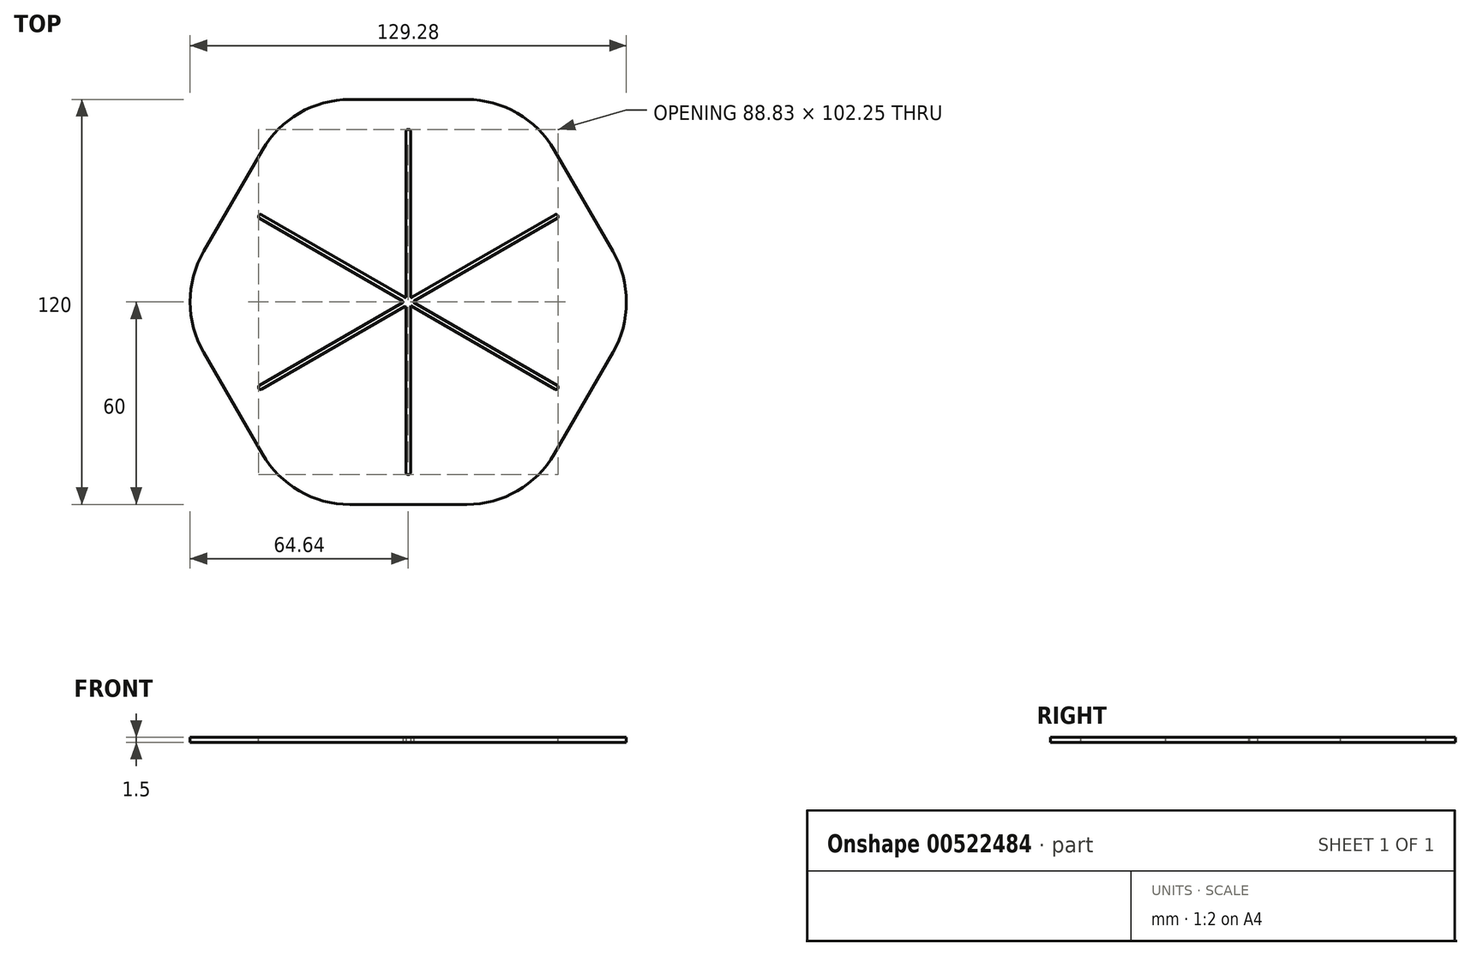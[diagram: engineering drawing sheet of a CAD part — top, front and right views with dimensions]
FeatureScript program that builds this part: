
annotation { "Feature Type Name" : "Feature", "Feature Type Description" : "" }
export const myFeature = defineFeature(function(context is Context, id is Id, definition is map)
    precondition{}
    {
        {
            var Q0;
            Q0=qCreatedBy(makeId("Top.planeOp"),FACE);
            var sketch = newSketch(context, id + "F0", { "sketchPlane" : qUnion([Q0])});
            skCircle(sketch, "E0.cCircle", {"center": v(0, 0) * mm, "radius": 60 * mm, "construction": true});
            skLineSegment(sketch, "E0.0", {"start": v(-34.64, 60) * mm, "end": v(34.64, 60) * mm});
            skLineSegment(sketch, "E0.1", {"start": v(34.64, 60) * mm, "end": v(69.28, 0) * mm});
            skLineSegment(sketch, "E0.2", {"start": v(69.28, 0) * mm, "end": v(34.64, -60) * mm});
            skLineSegment(sketch, "E0.3", {"start": v(34.64, -60) * mm, "end": v(-34.64, -60) * mm});
            skLineSegment(sketch, "E0.4", {"start": v(-34.64, -60) * mm, "end": v(-69.28, 0) * mm});
            skLineSegment(sketch, "E0.5", {"start": v(-69.28, 0) * mm, "end": v(-34.64, 60) * mm});
            skPoint(sketch, "E0.0.midPoint", {"position": v(0, 60) * mm});
            skLineSegment(sketch, "E1.bottom", {"start": v(0.65, -51.13) * mm, "end": v(-0.65, -51.13) * mm});
            skLineSegment(sketch, "E1.top", {"start": v(0.65, 51.13) * mm, "end": v(-0.65, 51.13) * mm});
            skLineSegment(sketch, "E1.left", {"start": v(0.65, -51.13) * mm, "end": v(0.65, -1.13) * mm});
            skLineSegment(sketch, "E1.right", {"start": v(-0.65, -51.13) * mm, "end": v(-0.65, -1.13) * mm});
            skLineSegment(sketch, "E2.1.1", {"start": v(43.95, 26.13) * mm, "end": v(0.65, 1.13) * mm});
            skLineSegment(sketch, "E2.1.2", {"start": v(44.6, 25) * mm, "end": v(1.3, 0) * mm});
            skLineSegment(sketch, "E2.1.3", {"start": v(43.95, 26.13) * mm, "end": v(44.6, 25) * mm});
            skLineSegment(sketch, "E2.1.4", {"start": v(-44.6, -25) * mm, "end": v(-43.95, -26.13) * mm});
            skLineSegment(sketch, "E2.2.1", {"start": v(-44.6, 25) * mm, "end": v(-1.3, 0) * mm});
            skLineSegment(sketch, "E2.2.2", {"start": v(-43.95, 26.13) * mm, "end": v(-0.65, 1.13) * mm});
            skLineSegment(sketch, "E2.2.3", {"start": v(-44.6, 25) * mm, "end": v(-43.95, 26.13) * mm});
            skLineSegment(sketch, "E2.2.4", {"start": v(43.95, -26.13) * mm, "end": v(44.6, -25) * mm});
            skLineSegment(sketch, "E3.trimOffspring", {"start": v(1.3, 0) * mm, "end": v(44.6, -25) * mm});
            skLineSegment(sketch, "E4.trimOffspring", {"start": v(0.65, 1.13) * mm, "end": v(0.65, 51.13) * mm});
            skLineSegment(sketch, "E5.trimOffspring", {"start": v(-1.3, 0) * mm, "end": v(-44.6, -25) * mm});
            skLineSegment(sketch, "E6.trimOffspring", {"start": v(-0.65, 1.13) * mm, "end": v(-0.65, 51.13) * mm});
            skLineSegment(sketch, "E7.trimOffspring", {"start": v(0.65, -1.13) * mm, "end": v(43.95, -26.13) * mm});
            skLineSegment(sketch, "E8.trimOffspring", {"start": v(-0.65, -1.13) * mm, "end": v(-43.95, -26.13) * mm});
            skSolve(sketch);
        }
        {
            var Q0;
            Q0 = qSketchRegion(id + "F0", true);
            extrude(context, id + "F1", {"entities" : qUnion([Q0]), "depth" : 1.5 * mm, "offsetDistance" : 25 * mm});
        }
        {
            var Q0;
            Q0=makeQuery(id+"F1.opExtrude","SWEPT_EDGE",EDGE,{"disambiguationData":[OSD([sQuery(id+"F0.wireOp",EDGE,"E0.0"),sQuery(id+"F0.wireOp",EDGE,"E0.1")])]});
            var Q1;
            Q1=makeQuery(id+"F1.opExtrude","SWEPT_EDGE",EDGE,{"disambiguationData":[OSD([sQuery(id+"F0.wireOp",EDGE,"E0.1"),sQuery(id+"F0.wireOp",EDGE,"E0.2")])]});
            var Q2;
            Q2=makeQuery(id+"F1.opExtrude","SWEPT_EDGE",EDGE,{"disambiguationData":[OSD([sQuery(id+"F0.wireOp",EDGE,"E0.2"),sQuery(id+"F0.wireOp",EDGE,"E0.3")])]});
            var Q3;
            Q3=makeQuery(id+"F1.opExtrude","SWEPT_EDGE",EDGE,{"disambiguationData":[OSD([sQuery(id+"F0.wireOp",EDGE,"E0.3"),sQuery(id+"F0.wireOp",EDGE,"E0.4")])]});
            var Q4;
            Q4=makeQuery(id+"F1.opExtrude","SWEPT_EDGE",EDGE,{"disambiguationData":[OSD([sQuery(id+"F0.wireOp",EDGE,"E0.4"),sQuery(id+"F0.wireOp",EDGE,"E0.5")])]});
            var Q5;
            Q5=makeQuery(id+"F1.opExtrude","SWEPT_EDGE",EDGE,{"disambiguationData":[OSD([sQuery(id+"F0.wireOp",EDGE,"E0.0"),sQuery(id+"F0.wireOp",EDGE,"E0.5")])]});
            fillet(context, id + "F2", {"entities" : qUnion([Q0, Q1, Q2, Q3, Q4, Q5]), "radius" : 30 * mm, "tangentPropagation" : true, "allowEdgeOverflow" : false});
        }
        {
            var Q0;
            Q0=makeQuery(id+"F1.opExtrude","SWEPT_EDGE",EDGE,{"disambiguationData":[OSD([sQuery(id+"F0.wireOp",EDGE,"E2.2.4"),sQuery(id+"F0.wireOp",EDGE,"E7.trimOffspring")])]});
            var Q1;
            Q1=makeQuery(id+"F1.opExtrude","SWEPT_EDGE",EDGE,{"disambiguationData":[OSD([sQuery(id+"F0.wireOp",EDGE,"E2.2.4"),sQuery(id+"F0.wireOp",EDGE,"E3.trimOffspring")])]});
            var Q2;
            Q2=makeQuery(id+"F1.opExtrude","SWEPT_EDGE",EDGE,{"disambiguationData":[OSD([sQuery(id+"F0.wireOp",EDGE,"E2.1.1"),sQuery(id+"F0.wireOp",EDGE,"E2.1.3")])]});
            var Q3;
            Q3=makeQuery(id+"F1.opExtrude","SWEPT_EDGE",EDGE,{"disambiguationData":[OSD([sQuery(id+"F0.wireOp",EDGE,"E2.1.2"),sQuery(id+"F0.wireOp",EDGE,"E2.1.3")])]});
            var Q4;
            Q4=makeQuery(id+"F1.opExtrude","SWEPT_EDGE",EDGE,{"disambiguationData":[OSD([sQuery(id+"F0.wireOp",EDGE,"E1.top"),sQuery(id+"F0.wireOp",EDGE,"E6.trimOffspring")])]});
            var Q5;
            Q5=makeQuery(id+"F1.opExtrude","SWEPT_EDGE",EDGE,{"disambiguationData":[OSD([sQuery(id+"F0.wireOp",EDGE,"E1.top"),sQuery(id+"F0.wireOp",EDGE,"E4.trimOffspring")])]});
            var Q6;
            Q6=makeQuery(id+"F1.opExtrude","SWEPT_EDGE",EDGE,{"disambiguationData":[OSD([sQuery(id+"F0.wireOp",EDGE,"E2.2.1"),sQuery(id+"F0.wireOp",EDGE,"E2.2.3")])]});
            var Q7;
            Q7=makeQuery(id+"F1.opExtrude","SWEPT_EDGE",EDGE,{"disambiguationData":[OSD([sQuery(id+"F0.wireOp",EDGE,"E2.2.2"),sQuery(id+"F0.wireOp",EDGE,"E2.2.3")])]});
            var Q8;
            Q8=makeQuery(id+"F1.opExtrude","SWEPT_EDGE",EDGE,{"disambiguationData":[OSD([sQuery(id+"F0.wireOp",EDGE,"E2.1.4"),sQuery(id+"F0.wireOp",EDGE,"E8.trimOffspring")])]});
            var Q9;
            Q9=makeQuery(id+"F1.opExtrude","SWEPT_EDGE",EDGE,{"disambiguationData":[OSD([sQuery(id+"F0.wireOp",EDGE,"E2.1.4"),sQuery(id+"F0.wireOp",EDGE,"E5.trimOffspring")])]});
            var Q10;
            Q10=makeQuery(id+"F1.opExtrude","SWEPT_EDGE",EDGE,{"disambiguationData":[OSD([sQuery(id+"F0.wireOp",EDGE,"E1.bottom"),sQuery(id+"F0.wireOp",EDGE,"E1.right")])]});
            var Q11;
            Q11=makeQuery(id+"F1.opExtrude","SWEPT_EDGE",EDGE,{"disambiguationData":[OSD([sQuery(id+"F0.wireOp",EDGE,"E1.bottom"),sQuery(id+"F0.wireOp",EDGE,"E1.left")])]});
            fillet(context, id + "F3", {"entities" : qUnion([Q0, Q1, Q2, Q3, Q4, Q5, Q6, Q7, Q8, Q9, Q10, Q11]), "radius" : .5 * mm, "tangentPropagation" : true, "allowEdgeOverflow" : false});
        }
        {
            var Q0;
            Q0=makeQuery(id+"F1.opExtrude","SWEPT_EDGE",EDGE,{"disambiguationData":[OSD([sQuery(id+"F0.wireOp",EDGE,"E2.2.2"),sQuery(id+"F0.wireOp",EDGE,"E6.trimOffspring")])]});
            var Q1;
            Q1=makeQuery(id+"F1.opExtrude","SWEPT_EDGE",EDGE,{"disambiguationData":[OSD([sQuery(id+"F0.wireOp",EDGE,"E2.2.1"),sQuery(id+"F0.wireOp",EDGE,"E5.trimOffspring")])]});
            var Q2;
            Q2=makeQuery(id+"F1.opExtrude","SWEPT_EDGE",EDGE,{"disambiguationData":[OSD([sQuery(id+"F0.wireOp",EDGE,"E1.right"),sQuery(id+"F0.wireOp",EDGE,"E8.trimOffspring")])]});
            var Q3;
            Q3=makeQuery(id+"F1.opExtrude","SWEPT_EDGE",EDGE,{"disambiguationData":[OSD([sQuery(id+"F0.wireOp",EDGE,"E2.1.1"),sQuery(id+"F0.wireOp",EDGE,"E4.trimOffspring")])]});
            var Q4;
            Q4=makeQuery(id+"F1.opExtrude","SWEPT_EDGE",EDGE,{"disambiguationData":[OSD([sQuery(id+"F0.wireOp",EDGE,"E2.1.2"),sQuery(id+"F0.wireOp",EDGE,"E3.trimOffspring")])]});
            fillet(context, id + "F4", {"entities" : qUnion([Q0, Q1, Q2, Q3, Q4]), "radius" : .3 * mm, "tangentPropagation" : true, "allowEdgeOverflow" : false});
        }
    });
